# Revit family: PRD_FrankeWS_JntrlSnks_SludgeTrap_SIRW759
name_source: partatom
category: Plumbing Fixtures
revit_build: Autodesk Revit 2018 (Build: 20190510_1515(x64)
units: mm (PartAtom-declared; Revit-internal decimal feet)

## family parameters
Always vertical = Yes
Cut with Voids When Loaded = No
OmniClass Number = 23.45.05.14.99
OmniClass Title = Other Sanitary Washing Plumbing Fixtures
Part Type = Normal
Room Calculation Point = No
Round Connector Dimension = Use Diameter
Shared = No
Work Plane-Based = Yes

## types (1)
- SIRW759
    AssetType = Fixed
    BIMObjectName = PRD_AR_JanitorialSinks_SludgeTrap_SIRW759
    BodyMaterial = PRD_AR_MineralMaterial_Alpinewhite
    BowlDepth = 510.00 mm
    BowlHeight = 280.00 mm
    BowlWidth = 620.00 mm
    Category = Pr_40_20_96_44, Janitorial sinks
    Color = alpine white
    Default Elevation = 1219 mm
    Description = Sludge collecting basin made of MIRANIT resin-bonded mineral material with pore-free smooth surface (temperature-resistant up to 80°C). Large inner radii. Alpine white colour. Version with 2-chamber system with removable divider made of plastic material, overflow for a controlled outflow into a customer-provided floor drain. On lockable rolls. DN 50 overflow with PVC pipe elbow on the side. PVC pipe and pipe elbows including mounting material.
    DiameterNominal = 50  [stored 0.164042 ft]
    DrainSize = 50 mm  [stored 0.164042 ft]
    DrainerOrStorage = No
    DurationUnit = year
    Features = MIRANIT resin-bonded mineral material, alpine white colour
    Finish = High polished
    Grid = No
    GrossWeight = 43.00 kg
    IfcExportAs = IfcSanitaryTerminalType
    IfcExportType = SINK
    IntegralAccessories = PVC pipe and pipe elbows including mounting material
    Manufacturer = KWC Group AG
    ManufacturerName = KWC Group AG
    ManufacturerURL = www.kwc.com
    Material = Mineral material
    MaterialCode = Miranit
    MaterialCodeGrid = Miranit
    Model = SIRW759
    ModelNumber = 2000102726
    ModelReference = SIRW759
    Mounting = OTHER
    MountingOffset = 0 mm  [stored 0 ft]
    NBSDescription = Janitorial units
    NBSReference = 45-35-70/401
    Name = Sludge trap SIRW759
    NetWeight = 40.80 kg
    NominalDepth = 550 mm
    NominalHeight = 370 mm  [stored 1.21391 ft]
    NominalWidth = 660 mm
    Overflow = Yes
    ProductCode = 207.0638.383
    ProductInformation = https://pim.kwc.com
    RearUpstand = No
    SinkType = OTHER
    Size = 660 x 300/370 x 550 mm (W x H x D)
    Sump = Yes
    TapLedge = No
    TypeOfMounting = No mounting
    TypeOfUtilitySink = Multi purpose sink
    URL = www.kwc.com
    Uniclass2015Code = Pr_40_20_96_44
    Uniclass2015Title = Janitorial sinks
    Uniclass2015Version = Products v1.17
    Version = 1
    WarrantyDurationUnit = year

note: [stored X ft] marks values corroborated as IEEE doubles in the binary element streams (Revit-internal decimal feet)

## geometry (parser evidence)
native form markers: Sweep x9
no freeform markers — native parametric forms only
